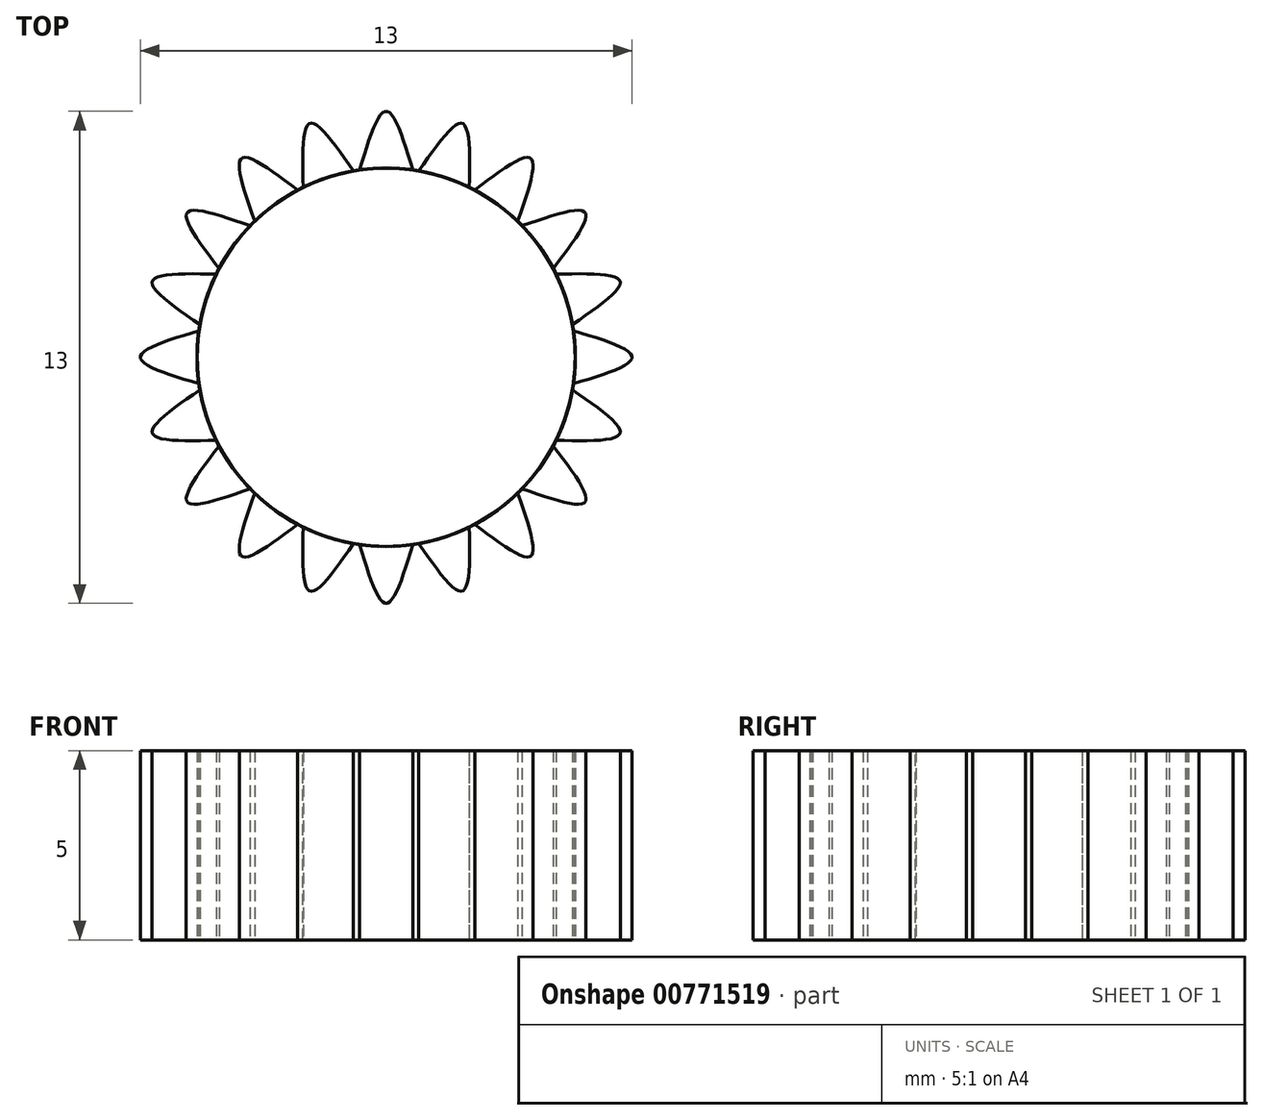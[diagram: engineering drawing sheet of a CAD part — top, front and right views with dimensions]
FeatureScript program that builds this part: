
annotation { "Feature Type Name" : "Feature", "Feature Type Description" : "" }
export const myFeature = defineFeature(function(context is Context, id is Id, definition is map)
    precondition{}
    {
        {
            var Q0;
            Q0=qCreatedBy(makeId("Top.planeOp"),FACE);
            var sketch = newSketch(context, id + "F0", { "sketchPlane" : qUnion([Q0])});
            skLineSegment(sketch, "E0", {"start": v(0, 0) * mm, "end": v(5, 0) * mm, "construction": true});
            skLineSegment(sketch, "E1", {"start": v(5, 0) * mm, "end": v(-6.5, 0) * mm, "construction": true});
            skCircle(sketch, "E2", {"center": v(0, 0) * mm, "radius": 5 * mm});
            skLineSegment(sketch, "E3", {"start": v(-5, 0) * mm, "end": v(-5, 0.7) * mm, "construction": true});
            skLineSegment(sketch, "E4", {"start": v(-5, 0.7) * mm, "end": v(-5, -0.7) * mm, "construction": true});
            skLineSegment(sketch, "E5", {"start": v(-5, -0.7) * mm, "end": v(-4.95, -0.7) * mm, "construction": true});
            skLineSegment(sketch, "E6", {"start": v(-4.95, -0.7) * mm, "end": v(-4.95, 0.7) * mm, "construction": true});
            skLineSegment(sketch, "E7", {"start": v(-4.95, 0.7) * mm, "end": v(-5, 0.7) * mm, "construction": true});
            skFitSpline(sketch, "E8", {"points": [v(-4.95, -0.7) * mm, v(-6.5, 0) * mm, v(-4.95, 0.7) * mm], "startDerivative": vector(-4.69, 1.4) * mm, "endDerivative": vector(4.69, 1.4) * mm});
            skSolve(sketch);
        }
        {
            var Q0;
            {var subQ0=sQuery(id+"F0.wireOp",EDGE,"E8");var subQ1=sQuery(id+"F0.wireOp",EDGE,"E2");var subQ2=makeQuery(id+"F0.imprint","INTERSECT",VERTEX,{"disambiguationData":[OD(0.0)],"derivedFrom":[subQ1,subQ0]});Q0=makeQuery(id+"F0.imprint","IMPRINT",FACE,{"disambiguationData":[TD([[makeQuery(id+"F0.imprint","IMPRINT",EDGE,{"disambiguationData":[TD([[subQ2,1.0]])],"derivedFrom":subQ1}),1.0]])]});}
            var Q1;
            {var subQ0=sQuery(id+"F0.wireOp",EDGE,"E8");Q1=makeQuery(id+"F0.imprint","IMPRINT",FACE,{"disambiguationData":[TD([[makeQuery(id+"F0.imprint","IMPRINT",EDGE,{"derivedFrom":subQ0}),-1.0]])]});}
            extrude(context, id + "F1", {"entities" : qUnion([Q0, Q1]), "depth" : 5 * mm, "offsetDistance" : 25 * mm});
        }
        {
            var Q0;
            Q0=makeQuery(id+"F1.opExtrude","SWEPT_BODY",BODY,{"disambiguationData":[OSD([sQuery(id+"F0.wireOp",EDGE,"E2"),sQuery(id+"F0.wireOp",EDGE,"E8")])]});
            var Q1;
            Q1=sQuery(id+"F0.wireOp",EDGE,"E2");
            circularPattern(context, id + "F2", {"entities" : qUnion([Q0]), "axis" : qUnion([Q1]), "angle" : 360 * degree, "instanceCount" : 20, "equalSpace" : true});
        }
    });
